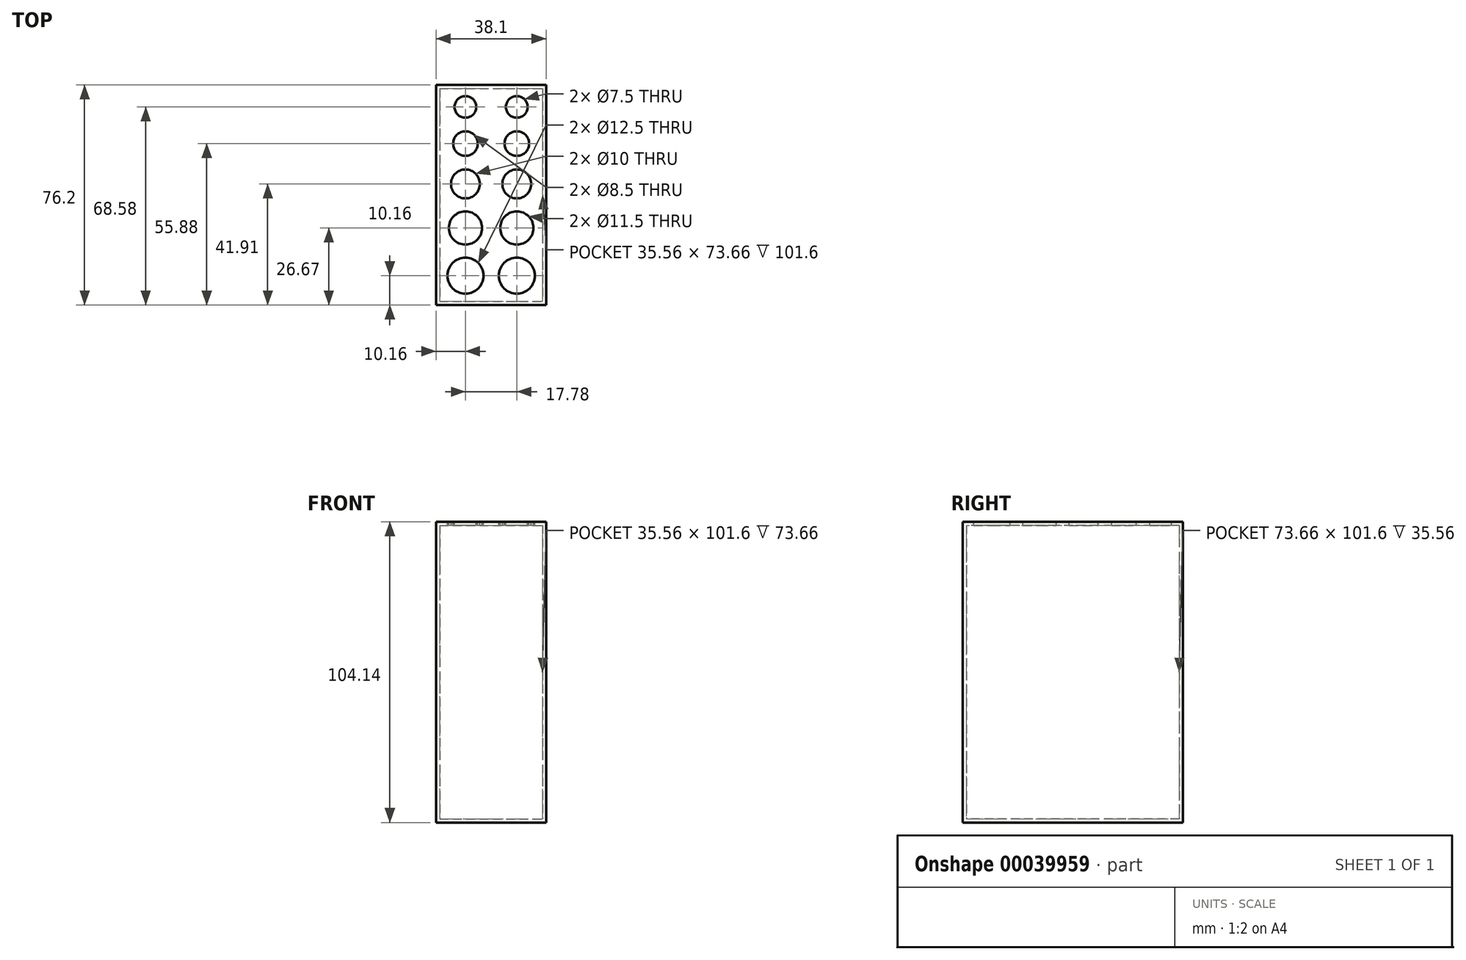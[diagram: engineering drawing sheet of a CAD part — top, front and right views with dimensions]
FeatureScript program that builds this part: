
annotation { "Feature Type Name" : "Feature", "Feature Type Description" : "" }
export const myFeature = defineFeature(function(context is Context, id is Id, definition is map)
    precondition{}
    {
        {
            var Q0;
            Q0=qCreatedBy(makeId("Top.planeOp"),FACE);
            var sketch = newSketch(context, id + "F0", { "sketchPlane" : qUnion([Q0])});
            skLineSegment(sketch, "E0.rect.bottom", {"start": v(19.05, -38.1) * mm, "end": v(-19.05, -38.1) * mm});
            skLineSegment(sketch, "E0.rect.top", {"start": v(19.05, 38.1) * mm, "end": v(-19.05, 38.1) * mm});
            skLineSegment(sketch, "E0.rect.left", {"start": v(19.05, -38.1) * mm, "end": v(19.05, 38.1) * mm});
            skLineSegment(sketch, "E0.rect.right", {"start": v(-19.05, -38.1) * mm, "end": v(-19.05, 38.1) * mm});
            skPoint(sketch, "E0.rect.middle", {"position": v(0, 0) * mm});
            skSolve(sketch);
        }
        {
            var Q0;
            Q0=makeQuery(id+"F0.imprint","IMPRINT",FACE,{"disambiguationData":[TD([[makeQuery(id+"F0.imprint","IMPRINT",EDGE,{"derivedFrom":sQuery(id+"F0.wireOp",EDGE,"E0.rect.bottom")}),-1.0]])]});
            extrude(context, id + "F1", {"entities" : qUnion([Q0]), "depth" : 1.27 * mm});
        }
        {
            var Q0;
            Q0=makeQuery(id+"F1.opExtrude","CAP_FACE",FACE,{"disambiguationData":[OSD([sQuery(id+"F0.wireOp",EDGE,"E0.rect.bottom"),sQuery(id+"F0.wireOp",EDGE,"E0.rect.top"),sQuery(id+"F0.wireOp",EDGE,"E0.rect.left"),sQuery(id+"F0.wireOp",EDGE,"E0.rect.right")])],"isStart":false});
            var sketch = newSketch(context, id + "F2", { "sketchPlane" : qUnion([Q0])});
            skLineSegment(sketch, "E1.bottom", {"start": v(-19.05, 38.1) * mm, "end": v(-17.78, 38.1) * mm});
            skLineSegment(sketch, "E1.top", {"start": v(-19.05, -38.1) * mm, "end": v(-17.78, -38.1) * mm});
            skLineSegment(sketch, "E1.left", {"start": v(-19.05, 38.1) * mm, "end": v(-19.05, -38.1) * mm});
            skLineSegment(sketch, "E1.right", {"start": v(-17.78, 38.1) * mm, "end": v(-17.78, -38.1) * mm});
            skLineSegment(sketch, "E2.bottom", {"start": v(-19.05, -38.1) * mm, "end": v(19.05, -38.1) * mm});
            skLineSegment(sketch, "E2.top", {"start": v(-19.05, -36.83) * mm, "end": v(19.05, -36.83) * mm});
            skLineSegment(sketch, "E2.left", {"start": v(-19.05, -38.1) * mm, "end": v(-19.05, -36.83) * mm});
            skLineSegment(sketch, "E2.right", {"start": v(19.05, -38.1) * mm, "end": v(19.05, -36.83) * mm});
            skLineSegment(sketch, "E3.bottom", {"start": v(-19.05, 38.1) * mm, "end": v(19.05, 38.1) * mm});
            skLineSegment(sketch, "E3.top", {"start": v(-19.05, 36.83) * mm, "end": v(19.05, 36.83) * mm});
            skLineSegment(sketch, "E3.left", {"start": v(-19.05, 38.1) * mm, "end": v(-19.05, 36.83) * mm});
            skLineSegment(sketch, "E3.right", {"start": v(19.05, 38.1) * mm, "end": v(19.05, 36.83) * mm});
            skLineSegment(sketch, "E4.bottom", {"start": v(19.05, 38.1) * mm, "end": v(17.78, 38.1) * mm});
            skLineSegment(sketch, "E4.top", {"start": v(19.05, -38.1) * mm, "end": v(17.78, -38.1) * mm});
            skLineSegment(sketch, "E4.left", {"start": v(19.05, 38.1) * mm, "end": v(19.05, -38.1) * mm});
            skLineSegment(sketch, "E4.right", {"start": v(17.78, 38.1) * mm, "end": v(17.78, -38.1) * mm});
            skSolve(sketch);
        }
        {
            var Q0;
            Q0 = qSketchRegion(id + "F2", true);
            extrude(context, id + "F3", {"entities" : qUnion([Q0]), "operationType" : NewBodyOperationType.ADD, "depth" : 101.6 * mm});
        }
        {
            var Q0;
            Q0=makeQuery(id+"F3.opExtrude","CAP_FACE",FACE,{"disambiguationData":[OSD([sQuery(id+"F2.wireOp",EDGE,"E1.left"),sQuery(id+"F2.wireOp",EDGE,"E1.right"),sQuery(id+"F2.wireOp",EDGE,"E2.bottom"),sQuery(id+"F2.wireOp",EDGE,"E2.top"),sQuery(id+"F2.wireOp",EDGE,"E2.left"),sQuery(id+"F2.wireOp",EDGE,"E3.bottom"),sQuery(id+"F2.wireOp",EDGE,"E3.top"),sQuery(id+"F2.wireOp",EDGE,"E3.left"),sQuery(id+"F2.wireOp",EDGE,"E4.bottom"),sQuery(id+"F2.wireOp",EDGE,"E4.top"),sQuery(id+"F2.wireOp",EDGE,"E4.left"),sQuery(id+"F2.wireOp",EDGE,"E4.right")])],"isStart":false});
            var sketch = newSketch(context, id + "F4", { "sketchPlane" : qUnion([Q0])});
            skLineSegment(sketch, "E5.bottom", {"start": v(-19.05, 38.1) * mm, "end": v(19.05, 38.1) * mm});
            skLineSegment(sketch, "E5.top", {"start": v(-19.05, -38.1) * mm, "end": v(19.05, -38.1) * mm});
            skLineSegment(sketch, "E5.left", {"start": v(-19.05, 38.1) * mm, "end": v(-19.05, -38.1) * mm});
            skLineSegment(sketch, "E5.right", {"start": v(19.05, 38.1) * mm, "end": v(19.05, -38.1) * mm});
            skSolve(sketch);
        }
        {
            var Q0;
            Q0 = qSketchRegion(id + "F4", true);
            extrude(context, id + "F5", {"entities" : qUnion([Q0]), "operationType" : NewBodyOperationType.ADD, "depth" : 1.27 * mm});
        }
        {
            var Q0;
            Q0=makeQuery(id+"F5.opExtrude","CAP_FACE",FACE,{"disambiguationData":[OSD([sQuery(id+"F4.wireOp",EDGE,"E5.bottom"),sQuery(id+"F4.wireOp",EDGE,"E5.top"),sQuery(id+"F4.wireOp",EDGE,"E5.left"),sQuery(id+"F4.wireOp",EDGE,"E5.right")])],"isStart":false});
            var sketch = newSketch(context, id + "F6", { "sketchPlane" : qUnion([Q0])});
            skSolve(sketch);
        }
        {
            var Q0;
            Q0=makeQuery(id+"F6.imprint","IMPRINT",FACE,{"disambiguationData":[TD([[makeQuery(id+"F6.imprint","IMPRINT",EDGE,{"derivedFrom":makeQuery(id+"F5.opExtrude","CAP_EDGE",EDGE,{"disambiguationData":[OSD([sQuery(id+"F4.wireOp",EDGE,"E5.bottom")])],"isStart":false})}),1.0]])]});
            var sketch = newSketch(context, id + "F7", { "sketchPlane" : qUnion([Q0])});
            skCircle(sketch, "E6", {"center": v(-8.89, 30.48) * mm, "radius": 3.75 * mm});
            skCircle(sketch, "E7", {"center": v(8.9, 30.48) * mm, "radius": 3.75 * mm});
            skCircle(sketch, "E8", {"center": v(-8.89, 17.78) * mm, "radius": 4.25 * mm});
            skCircle(sketch, "E9", {"center": v(8.9, 17.78) * mm, "radius": 4.25 * mm});
            skCircle(sketch, "E10", {"center": v(8.9, 3.81) * mm, "radius": 5 * mm});
            skCircle(sketch, "E11", {"center": v(-8.89, 3.81) * mm, "radius": 5 * mm});
            skCircle(sketch, "E12", {"center": v(-8.89, -11.43) * mm, "radius": 5.75 * mm});
            skCircle(sketch, "E13", {"center": v(8.9, -11.43) * mm, "radius": 5.75 * mm});
            skCircle(sketch, "E14", {"center": v(8.9, -27.94) * mm, "radius": 6.25 * mm});
            skCircle(sketch, "E15", {"center": v(-8.89, -27.94) * mm, "radius": 6.25 * mm});
            skSolve(sketch);
        }
        {
            var Q0;
            Q0 = qSketchRegion(id + "F7", true);
            extrude(context, id + "F8", {"entities" : qUnion([Q0]), "operationType" : NewBodyOperationType.REMOVE, "oppositeDirection" : true, "depth" : 25.4 * mm});
        }
    });
